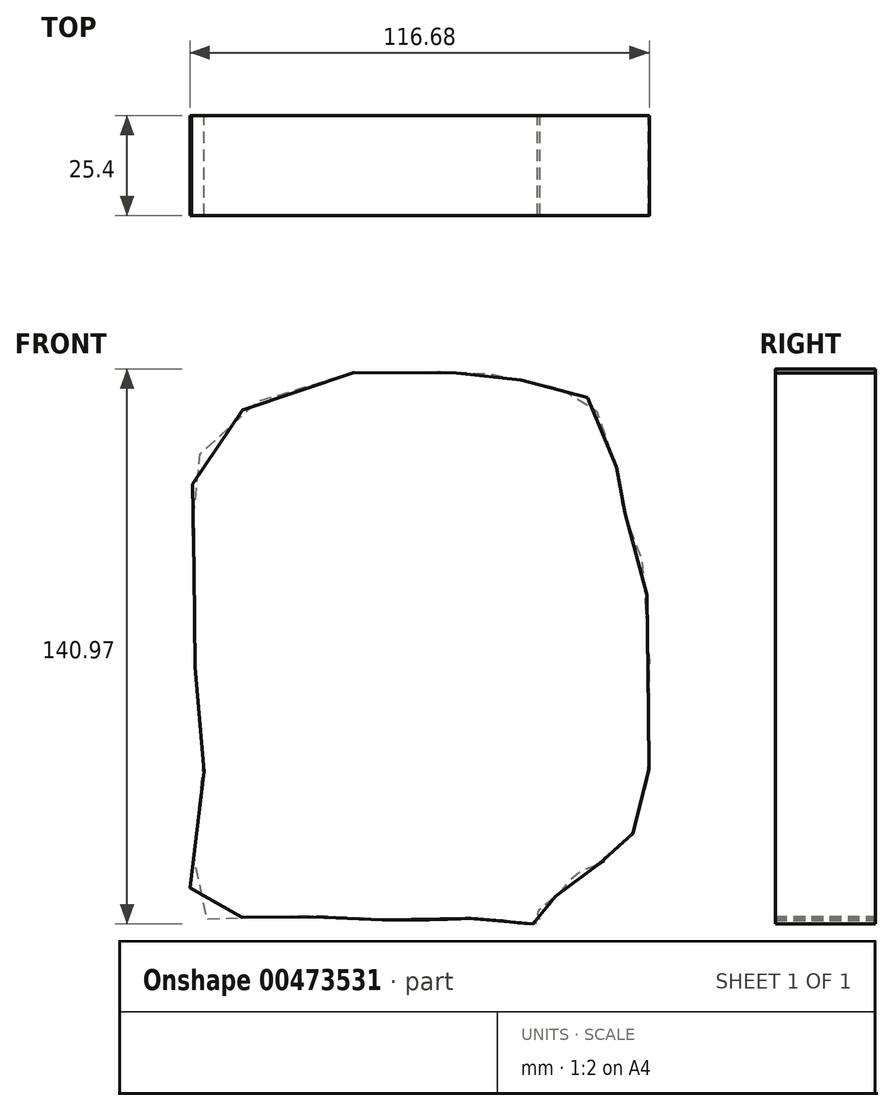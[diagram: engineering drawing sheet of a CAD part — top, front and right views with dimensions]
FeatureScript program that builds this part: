
annotation { "Feature Type Name" : "Feature", "Feature Type Description" : "" }
export const myFeature = defineFeature(function(context is Context, id is Id, definition is map)
    precondition{}
    {
        {
            var Q0;
            Q0=qCreatedBy(makeId("Front.planeOp"),FACE);
            var sketch = newSketch(context, id + "F0", { "sketchPlane" : qUnion([Q0])});
            skFitSpline(sketch, "E0", {"points": [v(0, -76.27) * mm, v(-10.36, -75.4) * mm, v(-25.04, -75.7) * mm, v(-35.11, -75.7) * mm, v(-47.49, -74.83) * mm, v(-45.76, -48.93) * mm, v(-46.91, -21.59) * mm, v(-47.78, 4.32) * mm, v(-48.06, 21) * mm, v(-46.91, 40.58) * mm, v(-31.37, 55.55) * mm, v(2.01, 63.6) * mm, v(21.3, 62.45) * mm, v(27.05, 62.45) * mm, v(45.47, 58.71) * mm, v(51.52, 56.99) * mm, v(57.56, 45.76) * mm, v(60.15, 33.96) * mm, v(60.44, 29.36) * mm, v(62.17, 26.2) * mm, v(66.77, 10.36) * mm, v(67.63, -23.31) * mm, v(67.63, -30.22) * mm, v(67.63, -38.85) * mm, v(65.04, -48.35) * mm, v(61.6, -58.71) * mm, v(56.4, -61.3) * mm, v(54.97, -62.17) * mm, v(49.8, -64.47) * mm, v(43.17, -71.09) * mm, v(39.43, -74.54) * mm, v(40, -76.84) * mm, v(30.22, -76.56) * mm, v(22.16, -75.98) * mm, v(21.59, -75.98) * mm, v(0, -76.27) * mm]});
            skSolve(sketch);
        }
        {
            var Q0;
            Q0 = qSketchRegion(id + "F0", true);
            extrude(context, id + "F1", {"entities" : qUnion([Q0]), "endBound" : BoundingType.SYMMETRIC, "depth" : 25.4 * mm});
        }
    });
